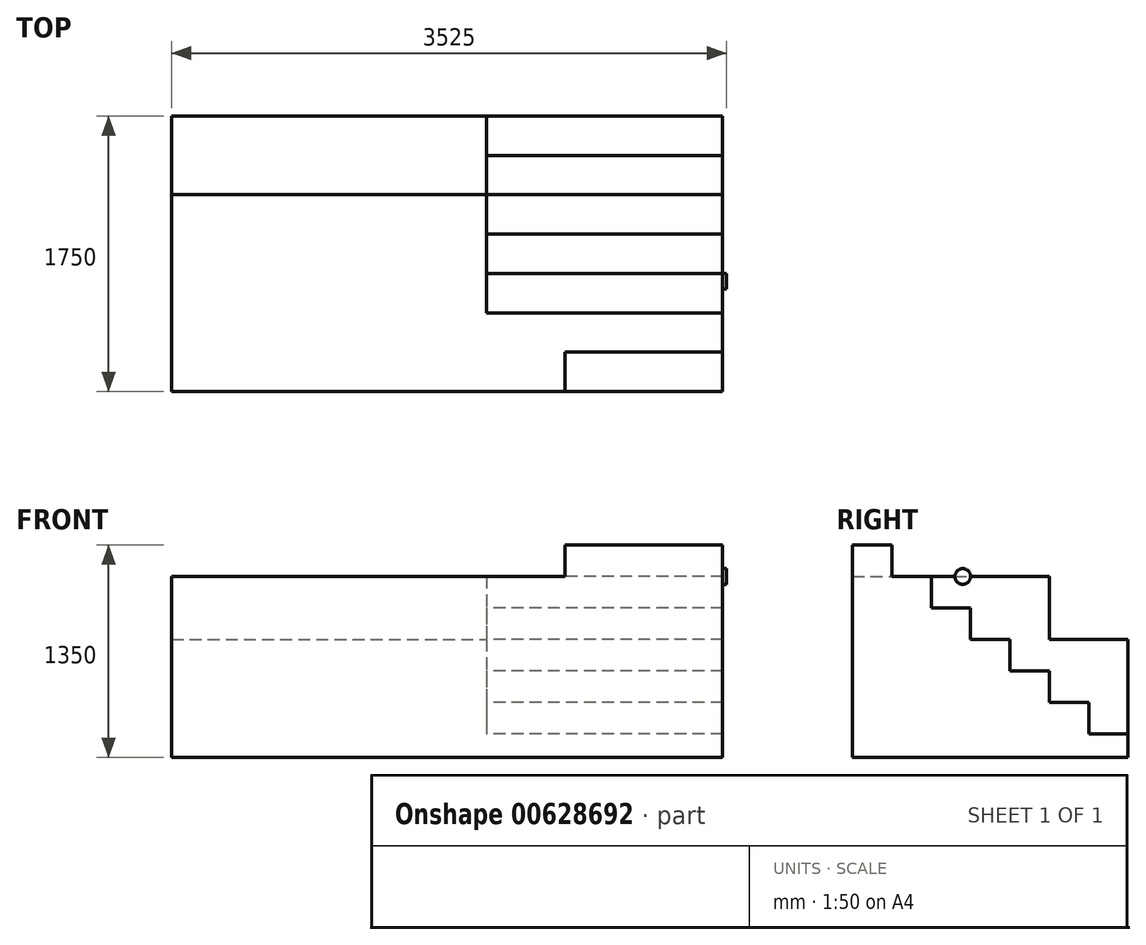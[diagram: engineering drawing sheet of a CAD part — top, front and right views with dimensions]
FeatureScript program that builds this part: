
annotation { "Feature Type Name" : "Feature", "Feature Type Description" : "" }
export const myFeature = defineFeature(function(context is Context, id is Id, definition is map)
    precondition{}
    {
        {
            var Q0;
            Q0=qCreatedBy(makeId("Top.planeOp"),FACE);
            var sketch = newSketch(context, id + "F0", { "sketchPlane" : qUnion([Q0])});
            skLineSegment(sketch, "E0.bottom", {"start": v(0, 0) * mm, "end": v(3500, 0) * mm});
            skLineSegment(sketch, "E0.top", {"start": v(0, 1750) * mm, "end": v(3500, 1750) * mm});
            skLineSegment(sketch, "E0.left", {"start": v(0, 0) * mm, "end": v(0, 1750) * mm});
            skLineSegment(sketch, "E0.right", {"start": v(3500, 0) * mm, "end": v(3500, 1750) * mm});
            skSolve(sketch);
        }
        {
            var Q0;
            Q0=makeQuery(id+"F0.imprint","IMPRINT",FACE,{"disambiguationData":[TD([[makeQuery(id+"F0.imprint","IMPRINT",EDGE,{"derivedFrom":sQuery(id+"F0.wireOp",EDGE,"E0.bottom")}),1.0]])]});
            extrude(context, id + "F1", {"entities" : qUnion([Q0]), "depth" : 150 * mm, "offsetDistance" : 25 * mm});
        }
        {
            var Q0;
            Q0=makeQuery(id+"F1.opExtrude","CAP_FACE",FACE,{"disambiguationData":[OSD([sQuery(id+"F0.wireOp",EDGE,"E0.bottom"),sQuery(id+"F0.wireOp",EDGE,"E0.top"),sQuery(id+"F0.wireOp",EDGE,"E0.left"),sQuery(id+"F0.wireOp",EDGE,"E0.right")])],"isStart":false});
            var sketch = newSketch(context, id + "F2", { "sketchPlane" : qUnion([Q0])});
            skLineSegment(sketch, "E1.bottom", {"start": v(3500, 0) * mm, "end": v(2000, 0) * mm});
            skLineSegment(sketch, "E1.top", {"start": v(3500, 1500) * mm, "end": v(2000, 1500) * mm});
            skLineSegment(sketch, "E1.left", {"start": v(3500, 0) * mm, "end": v(3500, 1500) * mm});
            skLineSegment(sketch, "E1.right", {"start": v(2000, 0) * mm, "end": v(2000, 1500) * mm});
            skSolve(sketch);
        }
        {
            var Q0;
            Q0=makeQuery(id+"F2.imprint","IMPRINT",FACE,{"disambiguationData":[TD([[makeQuery(id+"F2.imprint","IMPRINT",EDGE,{"derivedFrom":sQuery(id+"F2.wireOp",EDGE,"E1.bottom")}),1.0]])]});
            extrude(context, id + "F3", {"entities" : qUnion([Q0]), "operationType" : NewBodyOperationType.ADD, "depth" : 200 * mm, "offsetDistance" : 25 * mm});
        }
        {
            var Q0;
            Q0=makeQuery(id+"F3.opExtrude","CAP_FACE",FACE,{"disambiguationData":[OSD([sQuery(id+"F2.wireOp",EDGE,"E1.bottom"),sQuery(id+"F2.wireOp",EDGE,"E1.top"),sQuery(id+"F2.wireOp",EDGE,"E1.left"),sQuery(id+"F2.wireOp",EDGE,"E1.right")])],"isStart":false});
            var sketch = newSketch(context, id + "F4", { "sketchPlane" : qUnion([Q0])});
            skLineSegment(sketch, "E2.bottom", {"start": v(3500, 0) * mm, "end": v(2000, 0) * mm});
            skLineSegment(sketch, "E2.top", {"start": v(3500, 1250) * mm, "end": v(2000, 1250) * mm});
            skLineSegment(sketch, "E2.left", {"start": v(3500, 0) * mm, "end": v(3500, 1250) * mm});
            skLineSegment(sketch, "E2.right", {"start": v(2000, 0) * mm, "end": v(2000, 1250) * mm});
            skSolve(sketch);
        }
        {
            var Q0;
            Q0=makeQuery(id+"F4.imprint","IMPRINT",FACE,{"disambiguationData":[TD([[makeQuery(id+"F4.imprint","IMPRINT",EDGE,{"derivedFrom":sQuery(id+"F4.wireOp",EDGE,"E2.bottom")}),1.0]])]});
            extrude(context, id + "F5", {"entities" : qUnion([Q0]), "operationType" : NewBodyOperationType.ADD, "depth" : 200 * mm, "offsetDistance" : 25 * mm});
        }
        {
            var Q0;
            Q0=makeQuery(id+"F5.opExtrude","CAP_FACE",FACE,{"disambiguationData":[OSD([sQuery(id+"F4.wireOp",EDGE,"E2.bottom"),sQuery(id+"F4.wireOp",EDGE,"E2.top"),sQuery(id+"F4.wireOp",EDGE,"E2.left"),sQuery(id+"F4.wireOp",EDGE,"E2.right")])],"isStart":false});
            var sketch = newSketch(context, id + "F6", { "sketchPlane" : qUnion([Q0])});
            skLineSegment(sketch, "E3.bottom", {"start": v(3500, 0) * mm, "end": v(2000, 0) * mm});
            skLineSegment(sketch, "E3.top", {"start": v(3500, 1000) * mm, "end": v(2000, 1000) * mm});
            skLineSegment(sketch, "E3.left", {"start": v(3500, 0) * mm, "end": v(3500, 1000) * mm});
            skLineSegment(sketch, "E3.right", {"start": v(2000, 0) * mm, "end": v(2000, 1000) * mm});
            skSolve(sketch);
        }
        {
            var Q0;
            Q0=makeQuery(id+"F6.imprint","IMPRINT",FACE,{"disambiguationData":[TD([[makeQuery(id+"F6.imprint","IMPRINT",EDGE,{"derivedFrom":sQuery(id+"F6.wireOp",EDGE,"E3.bottom")}),1.0]])]});
            extrude(context, id + "F7", {"entities" : qUnion([Q0]), "operationType" : NewBodyOperationType.ADD, "depth" : 200 * mm, "offsetDistance" : 25 * mm});
        }
        {
            var Q0;
            Q0=makeQuery(id+"F7.opExtrude","CAP_FACE",FACE,{"disambiguationData":[OSD([sQuery(id+"F6.wireOp",EDGE,"E3.bottom"),sQuery(id+"F6.wireOp",EDGE,"E3.top"),sQuery(id+"F6.wireOp",EDGE,"E3.left"),sQuery(id+"F6.wireOp",EDGE,"E3.right")])],"isStart":false});
            var sketch = newSketch(context, id + "F8", { "sketchPlane" : qUnion([Q0])});
            skLineSegment(sketch, "E4.bottom", {"start": v(3500, 0) * mm, "end": v(2000, 0) * mm});
            skLineSegment(sketch, "E4.top", {"start": v(3500, 750) * mm, "end": v(2000, 750) * mm});
            skLineSegment(sketch, "E4.left", {"start": v(3500, 0) * mm, "end": v(3500, 750) * mm});
            skLineSegment(sketch, "E4.right", {"start": v(2000, 0) * mm, "end": v(2000, 750) * mm});
            skSolve(sketch);
        }
        {
            var Q0;
            Q0=makeQuery(id+"F8.imprint","IMPRINT",FACE,{"disambiguationData":[TD([[makeQuery(id+"F8.imprint","IMPRINT",EDGE,{"derivedFrom":sQuery(id+"F8.wireOp",EDGE,"E4.bottom")}),1.0]])]});
            extrude(context, id + "F9", {"entities" : qUnion([Q0]), "operationType" : NewBodyOperationType.ADD, "depth" : 200 * mm, "offsetDistance" : 25 * mm});
        }
        {
            var Q0;
            Q0=makeQuery(id+"F9.opExtrude","CAP_FACE",FACE,{"disambiguationData":[OSD([sQuery(id+"F8.wireOp",EDGE,"E4.bottom"),sQuery(id+"F8.wireOp",EDGE,"E4.top"),sQuery(id+"F8.wireOp",EDGE,"E4.left"),sQuery(id+"F8.wireOp",EDGE,"E4.right")])],"isStart":false});
            var sketch = newSketch(context, id + "F10", { "sketchPlane" : qUnion([Q0])});
            skLineSegment(sketch, "E5.bottom", {"start": v(3500, 0) * mm, "end": v(2000, 0) * mm});
            skLineSegment(sketch, "E5.top", {"start": v(3500, 500) * mm, "end": v(2000, 500) * mm});
            skLineSegment(sketch, "E5.left", {"start": v(3500, 0) * mm, "end": v(3500, 500) * mm});
            skLineSegment(sketch, "E5.right", {"start": v(2000, 0) * mm, "end": v(2000, 500) * mm});
            skSolve(sketch);
        }
        {
            var Q0;
            Q0=makeQuery(id+"F10.imprint","IMPRINT",FACE,{"disambiguationData":[TD([[makeQuery(id+"F10.imprint","IMPRINT",EDGE,{"derivedFrom":sQuery(id+"F10.wireOp",EDGE,"E5.bottom")}),1.0]])]});
            extrude(context, id + "F11", {"entities" : qUnion([Q0]), "operationType" : NewBodyOperationType.ADD, "depth" : 200 * mm, "offsetDistance" : 25 * mm});
        }
        {
            var Q0;
            Q0=makeQuery(id+"F11.boolean.opBoolean","MERGE",FACE,{"derivedFrom":[makeQuery(id+"F9.boolean.opBoolean","MERGE",FACE,{"derivedFrom":[makeQuery(id+"F7.boolean.opBoolean","MERGE",FACE,{"derivedFrom":[makeQuery(id+"F5.boolean.opBoolean","MERGE",FACE,{"derivedFrom":[makeQuery(id+"F3.boolean.opBoolean","MERGE",FACE,{"derivedFrom":[makeQuery(id+"F1.opExtrude","SWEPT_FACE",FACE,{"disambiguationData":[OSD([sQuery(id+"F0.wireOp",EDGE,"E0.right")])]}),makeQuery(id+"F3.opExtrude","SWEPT_FACE",FACE,{"disambiguationData":[OSD([sQuery(id+"F2.wireOp",EDGE,"E1.left")])]})]}),makeQuery(id+"F5.opExtrude","SWEPT_FACE",FACE,{"disambiguationData":[OSD([sQuery(id+"F4.wireOp",EDGE,"E2.left")])]})]}),makeQuery(id+"F7.opExtrude","SWEPT_FACE",FACE,{"disambiguationData":[OSD([sQuery(id+"F6.wireOp",EDGE,"E3.left")])]})]}),makeQuery(id+"F9.opExtrude","SWEPT_FACE",FACE,{"disambiguationData":[OSD([sQuery(id+"F8.wireOp",EDGE,"E4.left")])]})]}),makeQuery(id+"F11.opExtrude","SWEPT_FACE",FACE,{"disambiguationData":[OSD([sQuery(id+"F10.wireOp",EDGE,"E5.left")])]})]});
            var sketch = newSketch(context, id + "F12", { "sketchPlane" : qUnion([Q0])});
            skCircle(sketch, "E6", {"center": v(700, 1150) * mm, "radius": 50 * mm});
            skSolve(sketch);
        }
        {
            var Q0;
            Q0=makeQuery(id+"F12.imprint","IMPRINT",FACE,{"disambiguationData":[TD([[makeQuery(id+"F12.imprint","IMPRINT",EDGE,{"derivedFrom":sQuery(id+"F12.wireOp",EDGE,"E6")}),1.0]])]});
            extrude(context, id + "F13", {"entities" : qUnion([Q0]), "depth" : 25 * mm, "offsetDistance" : 25 * mm});
        }
        {
            var Q0;
            Q0=makeQuery(id+"F1.opExtrude","CAP_FACE",FACE,{"disambiguationData":[OSD([sQuery(id+"F0.wireOp",EDGE,"E0.bottom"),sQuery(id+"F0.wireOp",EDGE,"E0.top"),sQuery(id+"F0.wireOp",EDGE,"E0.left"),sQuery(id+"F0.wireOp",EDGE,"E0.right")])],"isStart":false});
            var sketch = newSketch(context, id + "F14", { "sketchPlane" : qUnion([Q0])});
            skLineSegment(sketch, "E7.bottom", {"start": v(0, 0) * mm, "end": v(2000, 0) * mm});
            skLineSegment(sketch, "E7.top", {"start": v(0, 1250) * mm, "end": v(2000, 1250) * mm});
            skLineSegment(sketch, "E7.left", {"start": v(0, 0) * mm, "end": v(0, 1250) * mm});
            skLineSegment(sketch, "E7.right", {"start": v(2000, 0) * mm, "end": v(2000, 1250) * mm});
            skSolve(sketch);
        }
        {
            var Q0;
            Q0=makeQuery(id+"F14.imprint","IMPRINT",FACE,{"disambiguationData":[TD([[makeQuery(id+"F14.imprint","IMPRINT",EDGE,{"derivedFrom":sQuery(id+"F14.wireOp",EDGE,"E7.bottom")}),1.0]])]});
            extrude(context, id + "F15", {"entities" : qUnion([Q0]), "operationType" : NewBodyOperationType.ADD, "depth" : 1000 * mm, "offsetDistance" : 25 * mm});
        }
        {
            var Q0;
            Q0=makeQuery(id+"F1.opExtrude","CAP_FACE",FACE,{"disambiguationData":[OSD([sQuery(id+"F0.wireOp",EDGE,"E0.bottom"),sQuery(id+"F0.wireOp",EDGE,"E0.top"),sQuery(id+"F0.wireOp",EDGE,"E0.left"),sQuery(id+"F0.wireOp",EDGE,"E0.right")])],"isStart":false});
            var sketch = newSketch(context, id + "F16", { "sketchPlane" : qUnion([Q0])});
            skLineSegment(sketch, "E8.bottom", {"start": v(2000, 1250) * mm, "end": v(0, 1250) * mm});
            skLineSegment(sketch, "E8.top", {"start": v(2000, 1750) * mm, "end": v(0, 1750) * mm});
            skLineSegment(sketch, "E8.left", {"start": v(2000, 1250) * mm, "end": v(2000, 1750) * mm});
            skLineSegment(sketch, "E8.right", {"start": v(0, 1250) * mm, "end": v(0, 1750) * mm});
            skSolve(sketch);
        }
        {
            var Q0;
            {var subQ2=sQuery(id+"F16.wireOp",EDGE,"E8.bottom");Q0=makeQuery(id+"F16.imprint","IMPRINT",FACE,{"disambiguationData":[TD([[makeQuery(id+"F16.imprint","IMPRINT",EDGE,{"derivedFrom":subQ2}),1.0]])]});}
            extrude(context, id + "F17", {"entities" : qUnion([Q0]), "operationType" : NewBodyOperationType.ADD, "depth" : 600 * mm, "offsetDistance" : 25 * mm});
        }
        {
            var Q0;
            Q0=makeQuery(id+"F15.boolean.opBoolean","MERGE",FACE,{"derivedFrom":[makeQuery(id+"F11.opExtrude","CAP_FACE",FACE,{"disambiguationData":[OSD([sQuery(id+"F10.wireOp",EDGE,"E5.bottom"),sQuery(id+"F10.wireOp",EDGE,"E5.top"),sQuery(id+"F10.wireOp",EDGE,"E5.left"),sQuery(id+"F10.wireOp",EDGE,"E5.right")])],"isStart":false}),makeQuery(id+"F15.opExtrude","CAP_FACE",FACE,{"disambiguationData":[OSD([sQuery(id+"F14.wireOp",EDGE,"E7.bottom"),sQuery(id+"F14.wireOp",EDGE,"E7.top"),sQuery(id+"F14.wireOp",EDGE,"E7.left"),sQuery(id+"F14.wireOp",EDGE,"E7.right")])],"isStart":false})]});
            var sketch = newSketch(context, id + "F18", { "sketchPlane" : qUnion([Q0])});
            skLineSegment(sketch, "E9.bottom", {"start": v(3500, 0) * mm, "end": v(2500, 0) * mm});
            skLineSegment(sketch, "E9.top", {"start": v(3500, 250) * mm, "end": v(2500, 250) * mm});
            skLineSegment(sketch, "E9.left", {"start": v(3500, 0) * mm, "end": v(3500, 250) * mm});
            skLineSegment(sketch, "E9.right", {"start": v(2500, 0) * mm, "end": v(2500, 250) * mm});
            skSolve(sketch);
        }
        {
            var Q0;
            Q0 = qSketchRegion(id + "F18", true);
            extrude(context, id + "F19", {"entities" : qUnion([Q0]), "operationType" : NewBodyOperationType.ADD, "depth" : 200 * mm, "offsetDistance" : 25 * mm});
        }
    });
